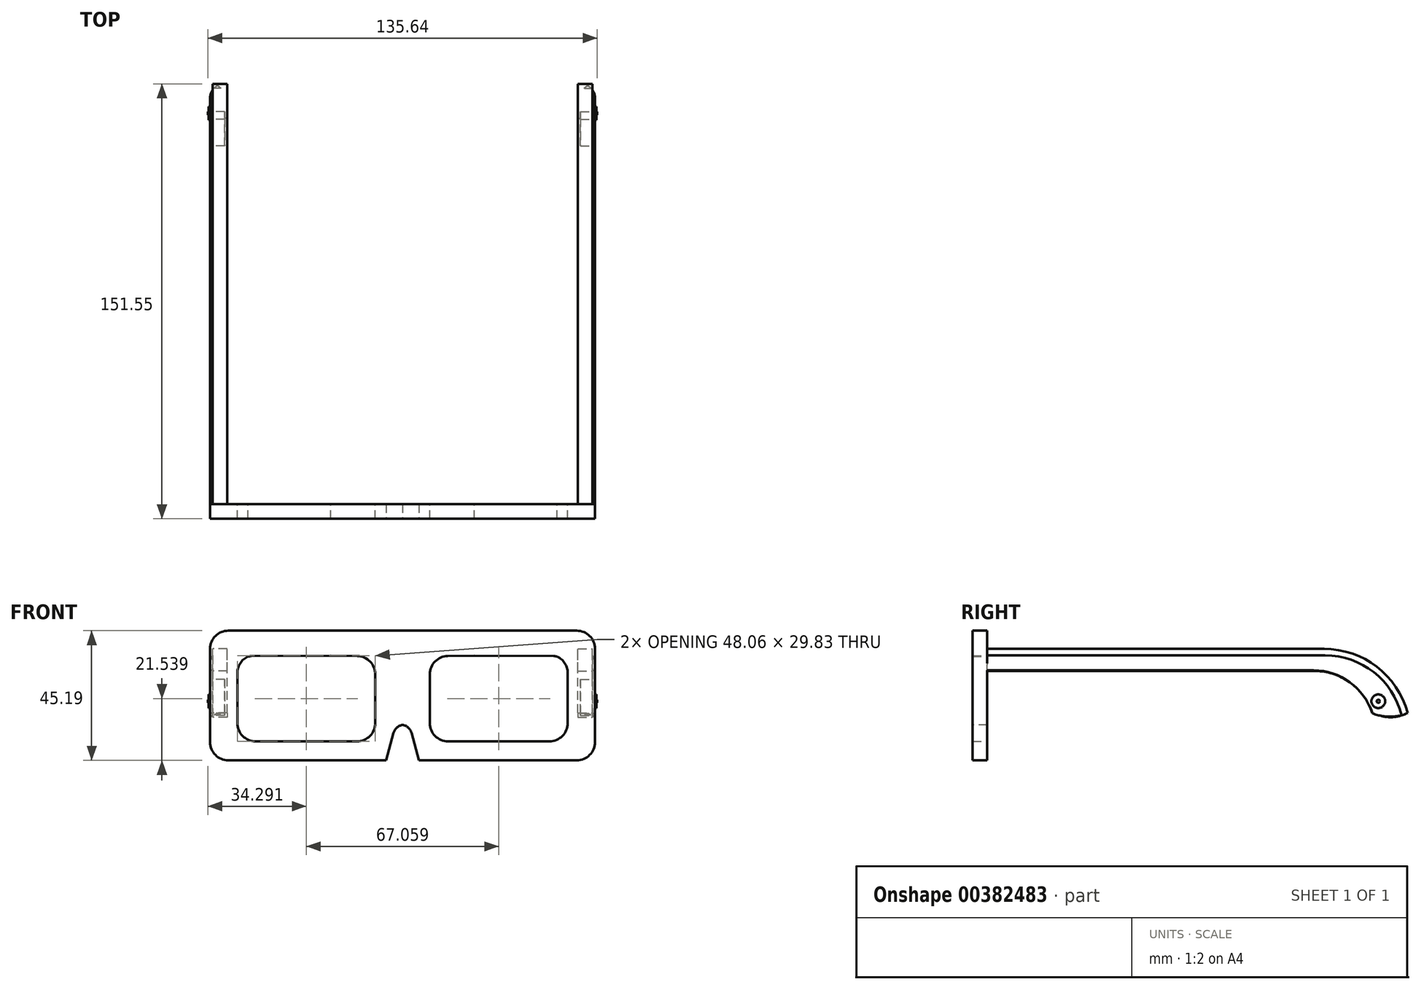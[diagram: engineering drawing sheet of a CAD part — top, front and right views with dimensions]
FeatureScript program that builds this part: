
annotation { "Feature Type Name" : "Feature", "Feature Type Description" : "" }
export const myFeature = defineFeature(function(context is Context, id is Id, definition is map)
    precondition{}
    {
        {
            var Q0;
            Q0=qCreatedBy(makeId("Front.planeOp"),FACE);
            var sketch = newSketch(context, id + "F0", { "sketchPlane" : qUnion([Q0])});
            skLineSegment(sketch, "E0", {"start": v(-67.06, 44.88) * mm, "end": v(-67.06, 12.4) * mm});
            skLineSegment(sketch, "E1", {"start": v(-60.7, 6.04) * mm, "end": v(59.85, 6.04) * mm});
            skLineSegment(sketch, "E2", {"start": v(66.2, 12.4) * mm, "end": v(66.2, 44.88) * mm});
            skLineSegment(sketch, "E3", {"start": v(59.85, 51.23) * mm, "end": v(-60.7, 51.23) * mm});
            skPoint(sketch, "E4.newPointA", {"position": v(-67.06, 51.23) * mm});
            skPoint(sketch, "E4.newPointB", {"position": v(-67.06, 52.96) * mm});
            skArc(sketch, "E4.filletArc", {"start": v(-60.7, 51.23) * mm, "mid": v(-65.2, 49.37) * mm, "end": v(-67.06, 44.88) * mm});
            skPoint(sketch, "E5.visualSharp", {"position": v(-67.06, 6.04) * mm});
            skArc(sketch, "E5.filletArc", {"start": v(-67.06, 12.4) * mm, "mid": v(-65.2, 7.9) * mm, "end": v(-60.7, 6.04) * mm});
            skPoint(sketch, "E6.visualSharp", {"position": v(66.2, 51.23) * mm});
            skArc(sketch, "E6.filletArc", {"start": v(66.2, 44.88) * mm, "mid": v(64.34, 49.37) * mm, "end": v(59.85, 51.23) * mm});
            skPoint(sketch, "E7.visualSharp", {"position": v(66.2, 6.04) * mm});
            skArc(sketch, "E7.filletArc", {"start": v(59.85, 6.04) * mm, "mid": v(64.34, 7.9) * mm, "end": v(66.2, 12.4) * mm});
            skSolve(sketch);
        }
        {
            var Q0;
            {var subQ0=sQuery(id+"F0.wireOp",EDGE,"E1");Q0=makeQuery(id+"F0.imprint","IMPRINT",FACE,{"disambiguationData":[TD([[makeQuery(id+"F0.imprint","IMPRINT",EDGE,{"derivedFrom":subQ0}),1.0]])]});}
            var sketch = newSketch(context, id + "F1", { "sketchPlane" : qUnion([Q0])});
            skLineSegment(sketch, "E8", {"start": v(-59, 36) * mm, "end": v(-59, 19.01) * mm});
            skLineSegment(sketch, "E9", {"start": v(-52.65, 12.66) * mm, "end": v(-12.97, 12.66) * mm});
            skLineSegment(sketch, "E10", {"start": v(-6.62, 19.01) * mm, "end": v(-6.62, 36.21) * mm});
            skLineSegment(sketch, "E11", {"start": v(-13, 42.56) * mm, "end": v(-52.69, 42.34) * mm});
            skPoint(sketch, "E12.visualSharp", {"position": v(-59, 42.3) * mm});
            skArc(sketch, "E12.filletArc", {"start": v(-52.69, 42.34) * mm, "mid": v(-57.15, 40.47) * mm, "end": v(-59, 36) * mm});
            skPoint(sketch, "E13.visualSharp", {"position": v(-59, 12.66) * mm});
            skArc(sketch, "E13.filletArc", {"start": v(-59, 19.01) * mm, "mid": v(-57.14, 14.52) * mm, "end": v(-52.65, 12.66) * mm});
            skPoint(sketch, "E14.visualSharp", {"position": v(-6.62, 12.66) * mm});
            skArc(sketch, "E14.filletArc", {"start": v(-12.97, 12.66) * mm, "mid": v(-8.48, 14.52) * mm, "end": v(-6.62, 19.01) * mm});
            skPoint(sketch, "E15.visualSharp", {"position": v(-6.62, 42.6) * mm});
            skArc(sketch, "E15.filletArc", {"start": v(-6.62, 36.21) * mm, "mid": v(-8.5, 40.71) * mm, "end": v(-13, 42.56) * mm});
            skSolve(sketch);
        }
        {
            var Q0;
            {var subQ0=sQuery(id+"F0.wireOp",EDGE,"E1");Q0=makeQuery(id+"F0.imprint","IMPRINT",FACE,{"disambiguationData":[TD([[makeQuery(id+"F0.imprint","IMPRINT",EDGE,{"derivedFrom":subQ0}),1.0]])]});}
            var sketch = newSketch(context, id + "F2", { "sketchPlane" : qUnion([Q0])});
            skLineSegment(sketch, "E16", {"start": v(9.5, 36.03) * mm, "end": v(9.5, 19.01) * mm});
            skLineSegment(sketch, "E17", {"start": v(15.85, 12.66) * mm, "end": v(51.21, 12.66) * mm});
            skLineSegment(sketch, "E18", {"start": v(57.56, 19.01) * mm, "end": v(57.56, 36.46) * mm});
            skLineSegment(sketch, "E19", {"start": v(51.14, 42.8) * mm, "end": v(15.77, 42.38) * mm});
            skPoint(sketch, "E20.visualSharp", {"position": v(9.5, 42.3) * mm});
            skArc(sketch, "E20.filletArc", {"start": v(15.77, 42.38) * mm, "mid": v(11.33, 40.5) * mm, "end": v(9.5, 36.03) * mm});
            skPoint(sketch, "E21.visualSharp", {"position": v(57.56, 42.88) * mm});
            skArc(sketch, "E21.filletArc", {"start": v(57.56, 36.46) * mm, "mid": v(55.67, 40.97) * mm, "end": v(51.14, 42.8) * mm});
            skPoint(sketch, "E22.visualSharp", {"position": v(57.56, 12.66) * mm});
            skArc(sketch, "E22.filletArc", {"start": v(51.21, 12.66) * mm, "mid": v(55.7, 14.52) * mm, "end": v(57.56, 19.01) * mm});
            skPoint(sketch, "E23.visualSharp", {"position": v(9.5, 12.66) * mm});
            skArc(sketch, "E23.filletArc", {"start": v(9.5, 19.01) * mm, "mid": v(11.36, 14.52) * mm, "end": v(15.85, 12.66) * mm});
            skSolve(sketch);
        }
        {
            var Q0;
            Q0 = qSketchRegion(id + "F0", true);
            extrude(context, id + "F3", {"entities" : qUnion([Q0]), "depth" : 5.08 * mm});
        }
        {
            var Q0;
            Q0 = qSketchRegion(id + "F1", true);
            extrude(context, id + "F4", {"entities" : qUnion([Q0]), "operationType" : NewBodyOperationType.REMOVE, "depth" : 25.4 * mm});
        }
        {
            var Q0;
            Q0 = qSketchRegion(id + "F2", true);
            extrude(context, id + "F5", {"entities" : qUnion([Q0]), "operationType" : NewBodyOperationType.REMOVE, "depth" : 25.4 * mm});
        }
        {
            var Q0;
            Q0=makeQuery(id+"F3.opExtrude","CAP_FACE",FACE,{"disambiguationData":[OSD([sQuery(id+"F0.wireOp",EDGE,"E0"),sQuery(id+"F0.wireOp",EDGE,"E1"),sQuery(id+"F0.wireOp",EDGE,"E2"),sQuery(id+"F0.wireOp",EDGE,"E3"),sQuery(id+"F0.wireOp",EDGE,"E4.filletArc"),sQuery(id+"F0.wireOp",EDGE,"E5.filletArc"),sQuery(id+"F0.wireOp",EDGE,"E6.filletArc"),sQuery(id+"F0.wireOp",EDGE,"E7.filletArc")])],"isStart":false});
            var sketch = newSketch(context, id + "F6", { "sketchPlane" : qUnion([Q0])});
            skPoint(sketch, "E24.startSnap0", {"position": v(-8.48, 14.52) * mm});
            skLineSegment(sketch, "E25", {"start": v(-5.76, 6.04) * mm, "end": v(-3.17, 15.54) * mm});
            skArc(sketch, "E26", {"start": v(0, 18.42) * mm, "mid": v(-2, 17.44) * mm, "end": v(-3.17, 15.54) * mm});
            skLineSegment(sketch, "E27.MirrorCS", {"start": v(5.76, 6.04) * mm, "end": v(3.17, 15.54) * mm});
            skArc(sketch, "E28.MirrorCS", {"start": v(0, 18.42) * mm, "mid": v(2, 17.44) * mm, "end": v(3.17, 15.54) * mm});
            skSolve(sketch);
        }
        {
            var Q0;
            {var subQ1=sQuery(id+"F6.wireOp",EDGE,"E25");Q0=makeQuery(id+"F6.imprint","IMPRINT",FACE,{"disambiguationData":[TD([[makeQuery(id+"F6.imprint","IMPRINT",EDGE,{"derivedFrom":subQ1}),-1.0]])]});}
            extrude(context, id + "F7", {"entities" : qUnion([Q0]), "operationType" : NewBodyOperationType.REMOVE, "oppositeDirection" : true, "depth" : 25.4 * mm});
        }
        {
            var Q0;
            Q0=makeQuery(id+"F3.opExtrude","SWEPT_FACE",FACE,{"disambiguationData":[OSD([sQuery(id+"F0.wireOp",EDGE,"E2")])]});
            var sketch = newSketch(context, id + "F8", { "sketchPlane" : qUnion([Q0])});
            skLineSegment(sketch, "E29", {"start": v(0, 44.88) * mm, "end": v(95.62, 44.88) * mm});
            skLineSegment(sketch, "E30", {"start": v(99.5, 37.17) * mm, "end": v(0, 37.17) * mm});
            skLineSegment(sketch, "E31", {"start": v(95.62, 44.88) * mm, "end": v(117.38, 44.88) * mm});
            skArc(sketch, "E32", {"start": v(146.47, 22.6) * mm, "mid": v(135.7, 38.67) * mm, "end": v(117.38, 44.88) * mm});
            skArc(sketch, "E33", {"start": v(134.49, 22.6) * mm, "mid": v(140.48, 21.09) * mm, "end": v(146.47, 22.6) * mm});
            skLineSegment(sketch, "E34", {"start": v(99.5, 37.17) * mm, "end": v(113.95, 37.17) * mm});
            skArc(sketch, "E35", {"start": v(134.49, 22.6) * mm, "mid": v(126.54, 33.16) * mm, "end": v(113.95, 37.17) * mm});
            skSolve(sketch);
        }
        {
            var Q0;
            Q0=makeQuery(id+"F3.opExtrude","SWEPT_FACE",FACE,{"disambiguationData":[OSD([sQuery(id+"F0.wireOp",EDGE,"E0")])]});
            var sketch = newSketch(context, id + "F9", { "sketchPlane" : qUnion([Q0])});
            skLineSegment(sketch, "E36", {"start": v(0, 44.88) * mm, "end": v(-96.78, 44.88) * mm});
            skLineSegment(sketch, "E37", {"start": v(0, 37.41) * mm, "end": v(-99.65, 37.41) * mm});
            skLineSegment(sketch, "E38", {"start": v(-96.78, 44.88) * mm, "end": v(-117.73, 44.88) * mm});
            skArc(sketch, "E39", {"start": v(-117.73, 44.88) * mm, "mid": v(-135.98, 38.6) * mm, "end": v(-146.52, 22.45) * mm});
            skArc(sketch, "E40", {"start": v(-146.52, 22.45) * mm, "mid": v(-140.33, 21.25) * mm, "end": v(-134.14, 22.45) * mm});
            skArc(sketch, "E41", {"start": v(-113.7, 37.41) * mm, "mid": v(-126.35, 33.24) * mm, "end": v(-134.14, 22.45) * mm});
            skLineSegment(sketch, "E42", {"start": v(-113.7, 37.41) * mm, "end": v(-99.65, 37.41) * mm});
            skSolve(sketch);
        }
        {
            var Q0;
            {var subQ1=sQuery(id+"F8.wireOp",EDGE,"E29");Q0=makeQuery(id+"F8.imprint","IMPRINT",FACE,{"disambiguationData":[TD([[makeQuery(id+"F8.imprint","IMPRINT",EDGE,{"derivedFrom":subQ1}),-1.0]])]});}
            extrude(context, id + "F10", {"entities" : qUnion([Q0]), "operationType" : NewBodyOperationType.ADD, "oppositeDirection" : true, "depth" : 5.08 * mm});
        }
        {
            var Q0;
            {var subQ1=sQuery(id+"F9.wireOp",EDGE,"E36");Q0=makeQuery(id+"F9.imprint","IMPRINT",FACE,{"disambiguationData":[TD([[makeQuery(id+"F9.imprint","IMPRINT",EDGE,{"derivedFrom":subQ1}),1.0]])]});}
            extrude(context, id + "F11", {"entities" : qUnion([Q0]), "oppositeDirection" : true, "depth" : 5.08 * mm});
        }
        {
            var Q0;
            Q0=makeQuery(id+"F11.opExtrude","CAP_EDGE",EDGE,{"disambiguationData":[OSD([sQuery(id+"F9.wireOp",EDGE,"E39")])],"isStart":true});
            var Q1;
            Q1=makeQuery(id+"F11.opExtrude","CAP_EDGE",EDGE,{"disambiguationData":[OSD([sQuery(id+"F9.wireOp",EDGE,"E36"),sQuery(id+"F9.wireOp",EDGE,"E38")])],"isStart":true});
            var Q2;
            Q2=makeQuery(id+"F11.opExtrude","CAP_EDGE",EDGE,{"disambiguationData":[OSD([sQuery(id+"F9.wireOp",EDGE,"E36"),sQuery(id+"F9.wireOp",EDGE,"E38")])],"isStart":false});
            var Q3;
            Q3=makeQuery(id+"F11.opExtrude","CAP_EDGE",EDGE,{"disambiguationData":[OSD([sQuery(id+"F9.wireOp",EDGE,"E39")])],"isStart":false});
            fillet(context, id + "F12", {"entities" : qUnion([Q0, Q1, Q2, Q3]), "radius" : 5.08 * mm, "tangentPropagation" : true, "allowEdgeOverflow" : false});
        }
        {
            var Q0;
            Q0=makeQuery(id+"F11.opExtrude","SWEPT_BODY",BODY,{"disambiguationData":[OSD([sQuery(id+"F0.wireOp",EDGE,"E0"),sQuery(id+"F9.wireOp",EDGE,"E36"),sQuery(id+"F9.wireOp",EDGE,"E37"),sQuery(id+"F9.wireOp",EDGE,"E38"),sQuery(id+"F9.wireOp",EDGE,"E39"),sQuery(id+"F9.wireOp",EDGE,"E40"),sQuery(id+"F9.wireOp",EDGE,"E41"),sQuery(id+"F9.wireOp",EDGE,"E42")])]});
            var Q1;
            Q1=qCreatedBy(makeId("Right.planeOp"),FACE);
            mirror(context, id + "F13", {"operationType" : NewBodyOperationType.ADD, "entities" : qUnion([Q0]), "mirrorPlane" : qUnion([Q1])});
        }
        {
            var Q0;
            {var subQ0=sQuery(id+"F0.wireOp",EDGE,"E0");Q0=makeQuery(id+"F13.boolean.opBoolean","MERGE",FACE,{"derivedFrom":[makeQuery(id+"F3.opExtrude","SWEPT_FACE",FACE,{"disambiguationData":[OSD([subQ0])]}),makeQuery(id+"F11.opExtrude","CAP_FACE",FACE,{"disambiguationData":[OSD([subQ0,sQuery(id+"F9.wireOp",EDGE,"E36"),sQuery(id+"F9.wireOp",EDGE,"E37"),sQuery(id+"F9.wireOp",EDGE,"E38"),sQuery(id+"F9.wireOp",EDGE,"E39"),sQuery(id+"F9.wireOp",EDGE,"E40"),sQuery(id+"F9.wireOp",EDGE,"E41"),sQuery(id+"F9.wireOp",EDGE,"E42")])],"isStart":true})]});}
            var sketch = newSketch(context, id + "F14", { "sketchPlane" : qUnion([Q0])});
            skCircle(sketch, "E43", {"center": v(-136.25, 26.63) * mm, "radius": 2.38 * mm});
            skSolve(sketch);
        }
        {
            var Q0;
            Q0 = qSketchRegion(id + "F14", true);
            extrude(context, id + "F15", {"entities" : qUnion([Q0]), "operationType" : NewBodyOperationType.ADD, "depth" : 0.5 * mm});
        }
        {
            var Q0;
            Q0=makeQuery(id+"F15.opExtrude","CAP_FACE",FACE,{"disambiguationData":[OSD([sQuery(id+"F14.wireOp",EDGE,"E43")])],"isStart":false});
            var sketch = newSketch(context, id + "F16", { "sketchPlane" : qUnion([Q0])});
            skCircle(sketch, "E44", {"center": v(-136.25, 26.63) * mm, "radius": 0.56 * mm});
            skSolve(sketch);
        }
        {
            var Q0;
            Q0 = qSketchRegion(id + "F16", true);
            extrude(context, id + "F17", {"entities" : qUnion([Q0]), "operationType" : NewBodyOperationType.ADD, "depth" : 0.25 * mm});
        }
        {
            var Q0;
            Q0=makeQuery(id+"F3.opExtrude","SWEPT_BODY",BODY,{"disambiguationData":[OSD([sQuery(id+"F0.wireOp",EDGE,"E0"),sQuery(id+"F0.wireOp",EDGE,"E1"),sQuery(id+"F0.wireOp",EDGE,"E2"),sQuery(id+"F0.wireOp",EDGE,"E3"),sQuery(id+"F0.wireOp",EDGE,"E4.filletArc"),sQuery(id+"F0.wireOp",EDGE,"E5.filletArc"),sQuery(id+"F0.wireOp",EDGE,"E6.filletArc"),sQuery(id+"F0.wireOp",EDGE,"E7.filletArc")])]});
            var Q1;
            Q1=qCreatedBy(makeId("Right.planeOp"),FACE);
            mirror(context, id + "F18", {"operationType" : NewBodyOperationType.ADD, "entities" : qUnion([Q0]), "mirrorPlane" : qUnion([Q1])});
        }
    });
